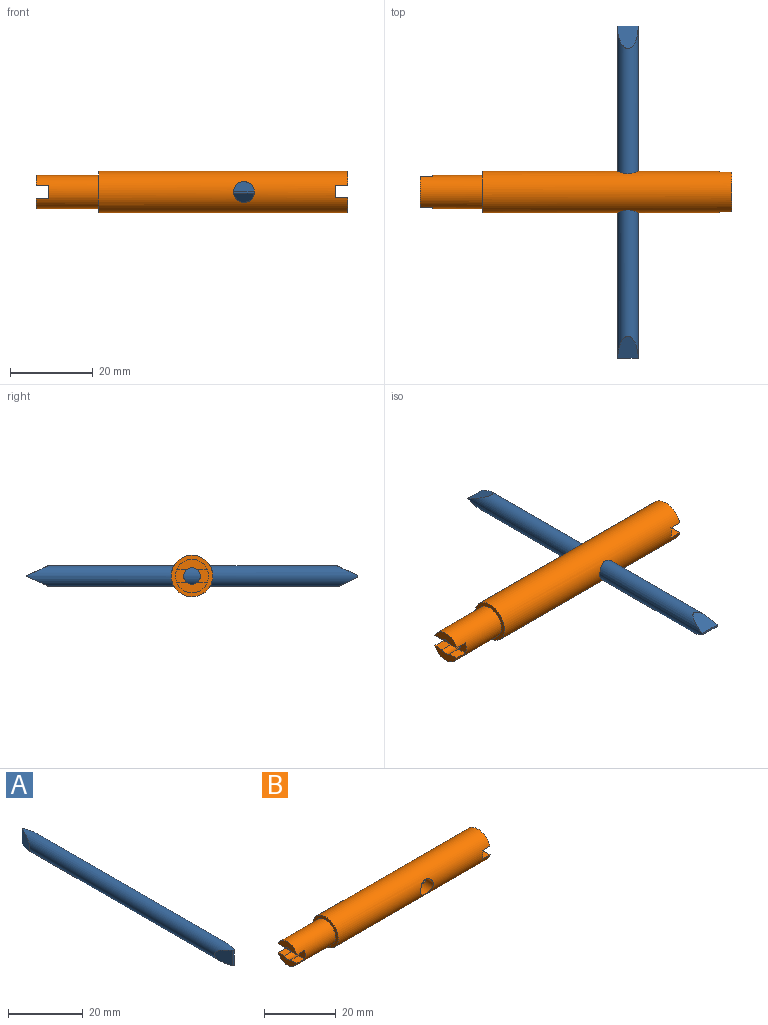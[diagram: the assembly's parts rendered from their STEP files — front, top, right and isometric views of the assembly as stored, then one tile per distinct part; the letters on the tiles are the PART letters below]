
ASSEMBLY  parts=2 mates=1
PART A: 7 faces, bbox 5x80x5 mm
  f0: cylinder r=2.5mm len=80mm, axis (0,1,0), area 1155.7mm2, adj f1,f2,f3,f4,f5,f6
  f1: plane 5x0.45mm, normal (0,-1,0), area 2.3mm2, adj f0,f3,f4
  f2: plane 5x0.06mm, normal (0,1,0), area 0.3mm2, adj f0,f5,f6
  f3: plane 4.98x4.64mm, normal (-0.9,-0.44,0), area 19.7mm2, adj f0,f1
  f4: plane 5.24x4.98mm, normal (0.92,-0.4,0), area 21.9mm2, adj f0,f1
  f5: plane 5.43x5mm, normal (0.91,0.41,0), area 23.3mm2, adj f0,f2
  f6: plane 5.47x5mm, normal (-0.91,0.41,0), area 23.5mm2, adj f0,f2
PART B: 22 faces, bbox 75x10x10 mm
  f0: cylinder r=2mm len=48.5mm, axis (-1,0,0), area 582.4mm2, adj f2,f8,f15,f16,f17,f18,f19,f20
  f1: cylinder r=4mm len=15mm, axis (-1,0,0), area 358.5mm2, adj f2,f7,f8,f16,f17,f18,f19,f20
  f2: plane 7.42x2.5mm, normal (-1,0,0), area 12.5mm2, adj f0,f1,f16,f19
  f3: cylinder r=2mm len=23.49mm, axis (-1,0,0), area 269.2mm2, adj f4,f5,f9,f10,f11,f12,f13,f14
  f4: plane 9.62x3.64mm, normal (1,0,0), area 24.4mm2, adj f3,f6,f9,f12
  f5: plane 9.55x3.52mm, normal (1,0,0), area 23.6mm2, adj f3,f6,f10,f13
  f6: cylinder r=5mm len=60mm, axis (-1,0,0), area 1826.7mm2, adj f4,f5,f7,f9,f10,f11,f12,f13
  f7: plane 10x10mm, normal (-1,0,0), area 28.3mm2, adj f1,f6
  f8: plane 7.42x2.5mm, normal (-1,0,0), area 12.5mm2, adj f0,f1,f18,f20
  f9: plane 3.36x3mm, normal (0,0,1), area 10.1mm2, adj f3,f4,f6,f11
  f10: plane 3.45x3mm, normal (0,0,-1), area 10.4mm2, adj f3,f5,f6,f11
  f11: plane 3.68x2.88mm, normal (1,0,0), area 9mm2, adj f3,f6,f9,f10
  f12: plane 3.36x3mm, normal (0,0,1), area 10.1mm2, adj f3,f4,f6,f14
  f13: plane 3.45x3mm, normal (0,0,-1), area 10.4mm2, adj f3,f5,f6,f14
  f14: plane 3.68x2.88mm, normal (1,0,0), area 9mm2, adj f3,f6,f12,f13
  f15: cylinder r=2.5mm len=8.66mm, axis (0,-1,0), area 108.3mm2, adj f0,f3,f6
  f16: plane 3x2.39mm, normal (0,0,-1), area 7.2mm2, adj f0,f1,f2,f17
  f17: plane 3x2.68mm, normal (-1,0,0), area 6.3mm2, adj f0,f1,f16,f18
  f18: plane 3x2.39mm, normal (0,0,1), area 7.2mm2, adj f0,f1,f8,f17
  f19: plane 3x2.39mm, normal (0,0,-1), area 7.2mm2, adj f0,f1,f2,f21
  f20: plane 3x2.39mm, normal (0,0,1), area 7.2mm2, adj f0,f1,f8,f21
  f21: plane 3x2.68mm, normal (-1,0,0), area 6.3mm2, adj f0,f1,f19,f20
PLACE A rot(axis=(0,-1,0),90deg) t=(13.07,-71.16,99.03)mm
PLACE B t=(-36.94,-71.16,99.03)mm
MATE fastened A.f0 <-> B.f15  axis (0,1,0) through (13.07,-71.16,99.03)mm
